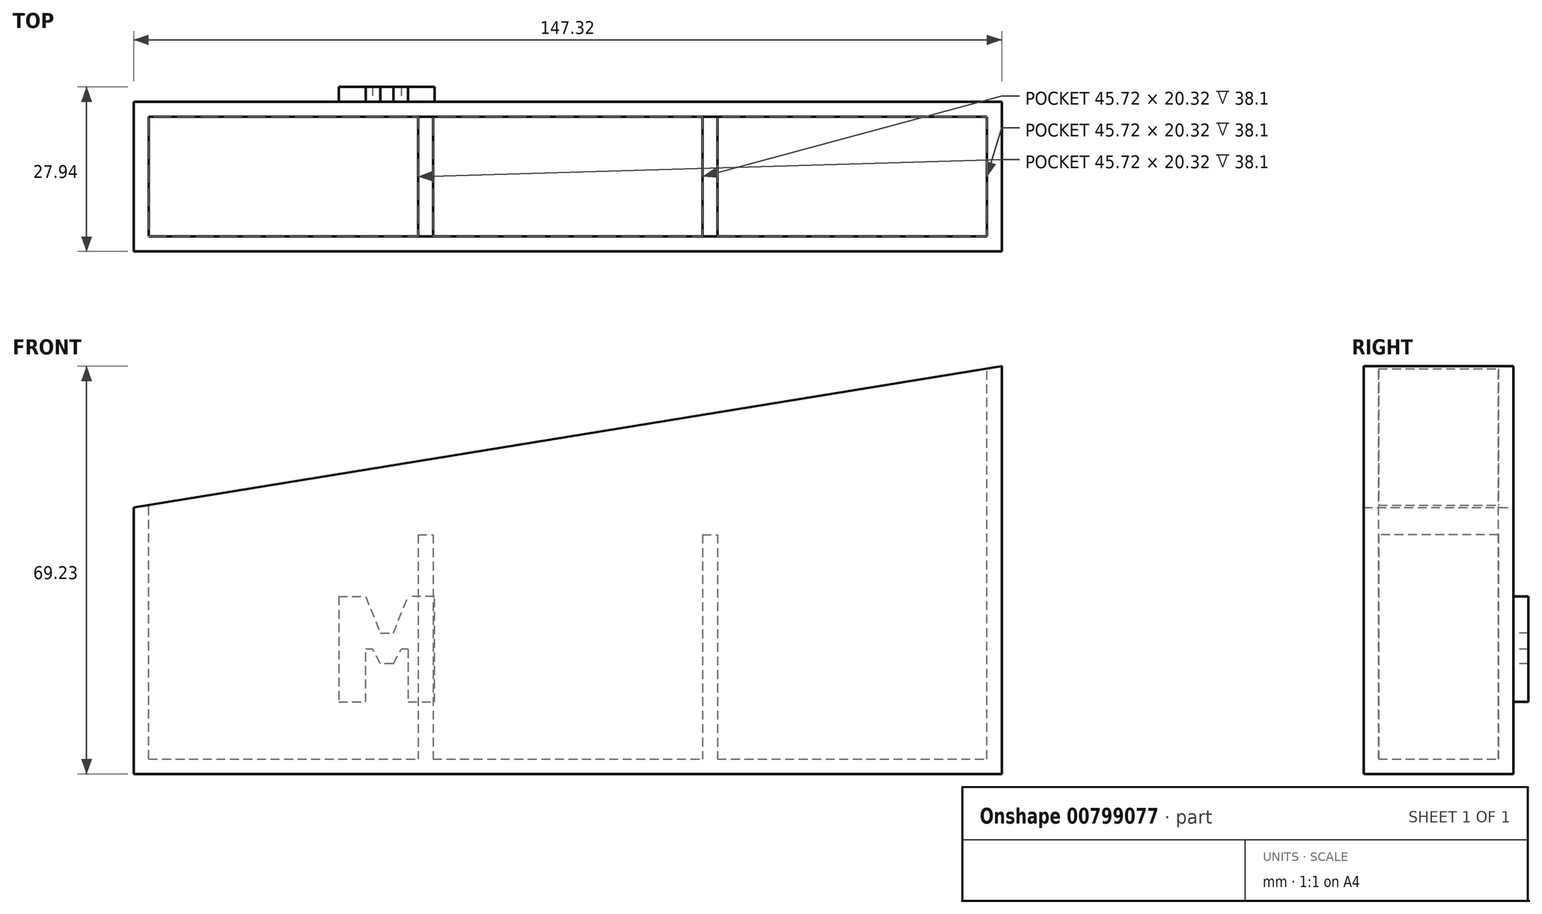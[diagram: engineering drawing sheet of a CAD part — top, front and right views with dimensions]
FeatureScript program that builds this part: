
annotation { "Feature Type Name" : "Feature", "Feature Type Description" : "" }
export const myFeature = defineFeature(function(context is Context, id is Id, definition is map)
    precondition{}
    {
        {
            var Q0;
            Q0=qCreatedBy(makeId("Front.planeOp"),FACE);
            var sketch = newSketch(context, id + "F0", { "sketchPlane" : qUnion([Q0])});
            skLineSegment(sketch, "E0.bottom", {"start": v(-66.06, -30.15) * mm, "end": v(81.26, -30.15) * mm});
            skLineSegment(sketch, "E0.left", {"start": v(-66.06, -30.15) * mm, "end": v(-66.06, 15.08) * mm});
            skLineSegment(sketch, "E0.right", {"start": v(81.26, -30.15) * mm, "end": v(81.26, 39.08) * mm});
            skLineSegment(sketch, "E1", {"start": v(81.26, 39.08) * mm, "end": v(-66.06, 15.08) * mm});
            skSolve(sketch);
        }
        {
            var Q0;
            Q0=makeQuery(id+"F0.imprint","IMPRINT",FACE,{"disambiguationData":[TD([[makeQuery(id+"F0.imprint","IMPRINT",EDGE,{"derivedFrom":sQuery(id+"F0.wireOp",EDGE,"E0.bottom")}),1.0]])]});
            extrude(context, id + "F1", {"entities" : qUnion([Q0]), "depth" : 25.4 * mm, "offsetDistance" : 25.4 * mm});
        }
        {
            var Q0;
            Q0=makeQuery(id+"F1.opExtrude","SWEPT_FACE",FACE,{"disambiguationData":[OSD([sQuery(id+"F0.wireOp",EDGE,"E1")])]});
            shell(context, id + "F2", {"entities" : qUnion([Q0]), "thickness" : 2.54 * mm});
        }
        {
            var Q0;
            Q0=makeQuery(id+"F2.opShell","OFFSET_FACE",FACE,{"disambiguationData":[OSD([sQuery(id+"F0.wireOp",EDGE,"E0.bottom")])]});
            var sketch = newSketch(context, id + "F3", { "sketchPlane" : qUnion([Q0])});
            skLineSegment(sketch, "E2", {"start": v(33, -2.54) * mm, "end": v(30.46, -2.54) * mm});
            skLineSegment(sketch, "E3", {"start": v(30.46, -2.54) * mm, "end": v(30.46, -22.86) * mm});
            skLineSegment(sketch, "E4", {"start": v(30.46, -22.86) * mm, "end": v(33, -22.86) * mm});
            skLineSegment(sketch, "E5", {"start": v(33, -22.86) * mm, "end": v(33, -2.54) * mm});
            skLineSegment(sketch, "E6", {"start": v(-15.26, -2.54) * mm, "end": v(-17.8, -2.54) * mm});
            skLineSegment(sketch, "E7", {"start": v(-17.8, -2.54) * mm, "end": v(-17.8, -22.86) * mm});
            skLineSegment(sketch, "E8", {"start": v(-17.8, -22.86) * mm, "end": v(-15.26, -22.86) * mm});
            skLineSegment(sketch, "E9", {"start": v(-15.26, -22.86) * mm, "end": v(-15.26, -2.54) * mm});
            skSolve(sketch);
        }
        {
            var Q0;
            Q0 = qSketchRegion(id + "F3", true);
            extrude(context, id + "F4", {"entities" : qUnion([Q0]), "operationType" : NewBodyOperationType.ADD, "depth" : 38.1 * mm, "offsetDistance" : 25.4 * mm});
        }
        {
            var Q0;
            Q0=qCreatedBy(makeId("Front.planeOp"),FACE);
            var sketch = newSketch(context, id + "F5", { "sketchPlane" : qUnion([Q0])});
            skLineSegment(sketch, "E10", {"start": v(-31.28, 0) * mm, "end": v(-31.28, -17.93) * mm});
            skLineSegment(sketch, "E11", {"start": v(-31.28, -17.93) * mm, "end": v(-26.7, -17.93) * mm});
            skLineSegment(sketch, "E12", {"start": v(-26.7, -17.93) * mm, "end": v(-26.7, -8.97) * mm});
            skPoint(sketch, "E12.endSnap0", {"position": v(-31.28, -8.97) * mm});
            skLineSegment(sketch, "E13", {"start": v(-19.48, -8.97) * mm, "end": v(-20.67, -8.97) * mm});
            skLineSegment(sketch, "E14", {"start": v(-19.48, -8.97) * mm, "end": v(-19.48, -17.93) * mm});
            skLineSegment(sketch, "E15", {"start": v(-19.48, -17.93) * mm, "end": v(-15.02, -17.93) * mm});
            skLineSegment(sketch, "E16", {"start": v(-15.02, -17.93) * mm, "end": v(-15.02, 0) * mm});
            skLineSegment(sketch, "E17", {"start": v(-15.02, 0) * mm, "end": v(-19.48, 0) * mm});
            skLineSegment(sketch, "E18", {"start": v(-31.28, 0) * mm, "end": v(-26.7, 0) * mm});
            skLineSegment(sketch, "E19", {"start": v(-26.7, 0) * mm, "end": v(-24.2, -6.2) * mm});
            skLineSegment(sketch, "E20", {"start": v(-21.98, -6.2) * mm, "end": v(-19.48, 0) * mm});
            skLineSegment(sketch, "E21", {"start": v(-24.2, -6.2) * mm, "end": v(-21.98, -6.2) * mm});
            skPoint(sketch, "E22.orphan", {"position": v(-23.1, -8.97) * mm});
            skLineSegment(sketch, "E23", {"start": v(-23.1, -11.42) * mm, "end": v(-24.2, -11.42) * mm});
            skLineSegment(sketch, "E24", {"start": v(-24.2, -11.42) * mm, "end": v(-21.98, -11.42) * mm});
            skLineSegment(sketch, "E25", {"start": v(-21.98, -11.42) * mm, "end": v(-20.67, -8.97) * mm});
            skLineSegment(sketch, "E26", {"start": v(-24.2, -11.42) * mm, "end": v(-25.5, -8.97) * mm});
            skPoint(sketch, "E27.orphan", {"position": v(-26.7, -6.73) * mm});
            skPoint(sketch, "E28.orphan", {"position": v(-19.48, -6.73) * mm});
            skLineSegment(sketch, "E29.trimOffspring", {"start": v(-25.5, -8.97) * mm, "end": v(-26.7, -8.97) * mm});
            skSolve(sketch);
        }
        {
            var Q0;
            Q0 = qSketchRegion(id + "F5", true);
            extrude(context, id + "F6", {"entities" : qUnion([Q0]), "operationType" : NewBodyOperationType.ADD, "oppositeDirection" : true, "depth" : 2.54 * mm, "offsetDistance" : 25.4 * mm});
        }
    });
